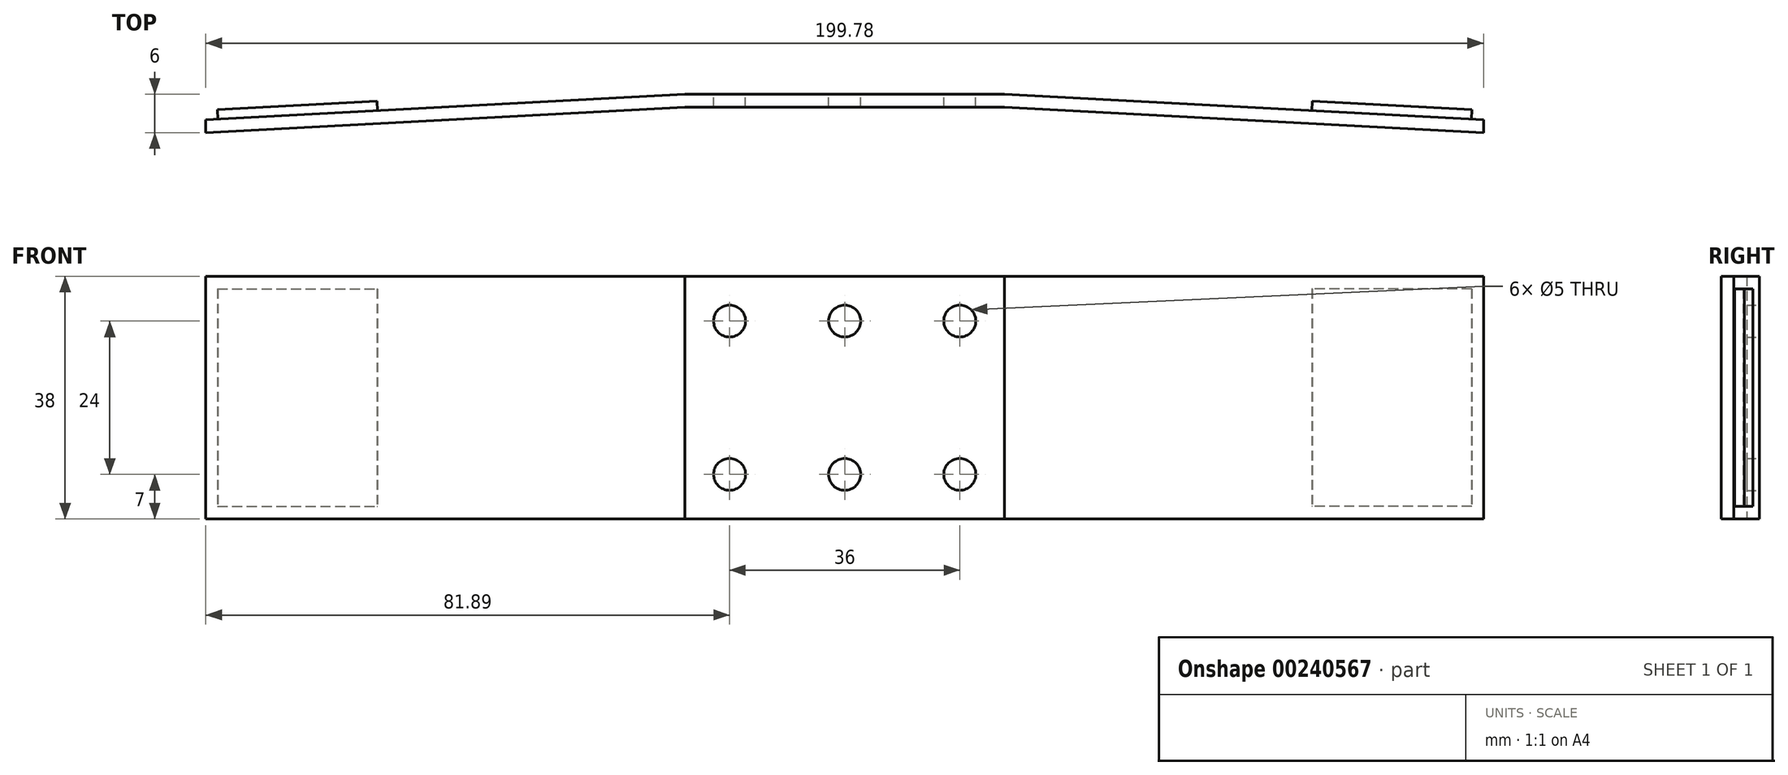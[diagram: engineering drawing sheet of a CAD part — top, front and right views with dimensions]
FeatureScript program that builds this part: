
annotation { "Feature Type Name" : "Feature", "Feature Type Description" : "" }
export const myFeature = defineFeature(function(context is Context, id is Id, definition is map)
    precondition{}
    {
        {
            var Q0;
            Q0=qCreatedBy(makeId("Top.planeOp"),FACE);
            var sketch = newSketch(context, id + "F0", { "sketchPlane" : qUnion([Q0])});
            skLineSegment(sketch, "E0", {"start": v(0, 0) * mm, "end": v(25, 0) * mm});
            skLineSegment(sketch, "E1", {"start": v(25, 0) * mm, "end": v(99.9, -4) * mm});
            skLineSegment(sketch, "E2", {"start": v(99.9, -4) * mm, "end": v(99.9, -6) * mm});
            skLineSegment(sketch, "E3", {"start": v(99.9, -6) * mm, "end": v(25, -2) * mm});
            skLineSegment(sketch, "E4", {"start": v(25, -2) * mm, "end": v(0, -2) * mm});
            skLineSegment(sketch, "E5", {"start": v(0, -2) * mm, "end": v(0, 0) * mm});
            skLineSegment(sketch, "E6", {"start": v(0, 0) * mm, "end": v(127.98, 0) * mm, "construction": true});
            skPoint(sketch, "E6.endSnap0", {"position": v(12.5, 0) * mm});
            skLineSegment(sketch, "E7.MirrorCS", {"start": v(-99.9, -4) * mm, "end": v(-99.9, -6) * mm});
            skPoint(sketch, "E8.MirrorP", {"position": v(-12.5, 0) * mm});
            skLineSegment(sketch, "E9.MirrorCS", {"start": v(-25, 0) * mm, "end": v(-99.9, -4) * mm});
            skLineSegment(sketch, "E10.MirrorCS", {"start": v(-25, -2) * mm, "end": v(0, -2) * mm});
            skLineSegment(sketch, "E11.MirrorCS", {"start": v(0, 0) * mm, "end": v(-25, 0) * mm});
            skLineSegment(sketch, "E12.MirrorCS", {"start": v(-99.9, -6) * mm, "end": v(-25, -2) * mm});
            skSolve(sketch);
        }
        {
            var Q0;
            Q0=makeQuery(id+"F0.imprint","IMPRINT",FACE,{"disambiguationData":[TD([[makeQuery(id+"F0.imprint","IMPRINT",EDGE,{"derivedFrom":sQuery(id+"F0.wireOp",EDGE,"E5")}),1.0]])]});
            var Q1;
            Q1=makeQuery(id+"F0.imprint","IMPRINT",FACE,{"disambiguationData":[TD([[makeQuery(id+"F0.imprint","IMPRINT",EDGE,{"derivedFrom":sQuery(id+"F0.wireOp",EDGE,"E0")}),-1.0]])]});
            extrude(context, id + "F1", {"entities" : qUnion([Q0, Q1]), "depth" : 38 * mm});
        }
        {
            var Q0;
            Q0=makeQuery(id+"F1.opExtrude","SWEPT_FACE",FACE,{"disambiguationData":[OSD([sQuery(id+"F0.wireOp",EDGE,"E0"),sQuery(id+"F0.wireOp",EDGE,"E11.MirrorCS")])]});
            var sketch = newSketch(context, id + "F2", { "sketchPlane" : qUnion([Q0])});
            skLineSegment(sketch, "E13", {"start": v(0, 38) * mm, "end": v(0, 0) * mm});
            skCircle(sketch, "E14", {"center": v(18, 31) * mm, "radius": 2.5 * mm});
            skCircle(sketch, "E15.0.1.0", {"center": v(18, 7) * mm, "radius": 2.5 * mm});
            skCircle(sketch, "E15.1.0.0", {"center": v(0, 31) * mm, "radius": 2.5 * mm});
            skCircle(sketch, "E15.1.1.0", {"center": v(0, 7) * mm, "radius": 2.5 * mm});
            skCircle(sketch, "E15.2.0.0", {"center": v(-18, 31) * mm, "radius": 2.5 * mm});
            skCircle(sketch, "E15.2.1.0", {"center": v(-18, 7) * mm, "radius": 2.5 * mm});
            skLineSegment(sketch, "E15.direction1", {"start": v(18, 31) * mm, "end": v(0, 31) * mm, "construction": true});
            skLineSegment(sketch, "E15.direction2", {"start": v(18, 31) * mm, "end": v(18, 7) * mm, "construction": true});
            skSolve(sketch);
        }
        {
            var Q0;
            Q0=makeQuery(id+"F1.opExtrude","SWEPT_FACE",FACE,{"disambiguationData":[OSD([sQuery(id+"F0.wireOp",EDGE,"E12.MirrorCS")])]});
            var sketch = newSketch(context, id + "F3", { "sketchPlane" : qUnion([Q0])});
            skLineSegment(sketch, "E16.bottom", {"start": v(-98.07, 36) * mm, "end": v(-73.07, 36) * mm});
            skLineSegment(sketch, "E16.top", {"start": v(-98.07, 2) * mm, "end": v(-73.07, 2) * mm});
            skLineSegment(sketch, "E16.left", {"start": v(-98.07, 36) * mm, "end": v(-98.07, 2) * mm});
            skLineSegment(sketch, "E16.right", {"start": v(-73.07, 36) * mm, "end": v(-73.07, 2) * mm});
            skSolve(sketch);
        }
        {
            var Q0;
            Q0=makeQuery(id+"F3.imprint","IMPRINT",FACE,{"disambiguationData":[TD([[makeQuery(id+"F3.imprint","IMPRINT",EDGE,{"derivedFrom":sQuery(id+"F3.wireOp",EDGE,"E16.bottom")}),-1.0]])]});
            extrude(context, id + "F4", {"entities" : qUnion([Q0]), "oppositeDirection" : true, "depth" : 3.5 * mm});
        }
        {
            var Q0;
            Q0=makeQuery(id+"F4.opExtrude","SWEPT_BODY",BODY,{"disambiguationData":[OSD([sQuery(id+"F3.wireOp",EDGE,"E16.bottom"),sQuery(id+"F3.wireOp",EDGE,"E16.top"),sQuery(id+"F3.wireOp",EDGE,"E16.left"),sQuery(id+"F3.wireOp",EDGE,"E16.right")])]});
            var Q1;
            Q1=qCreatedBy(makeId("Right.planeOp"),FACE);
            mirror(context, id + "F5", {"operationType" : NewBodyOperationType.ADD, "entities" : qUnion([Q0]), "mirrorPlane" : qUnion([Q1])});
        }
        {
            var Q0;
            Q0 = qSketchRegion(id + "F2", true);
            extrude(context, id + "F6", {"entities" : qUnion([Q0]), "operationType" : NewBodyOperationType.REMOVE, "oppositeDirection" : true, "depth" : 25 * mm});
        }
    });
